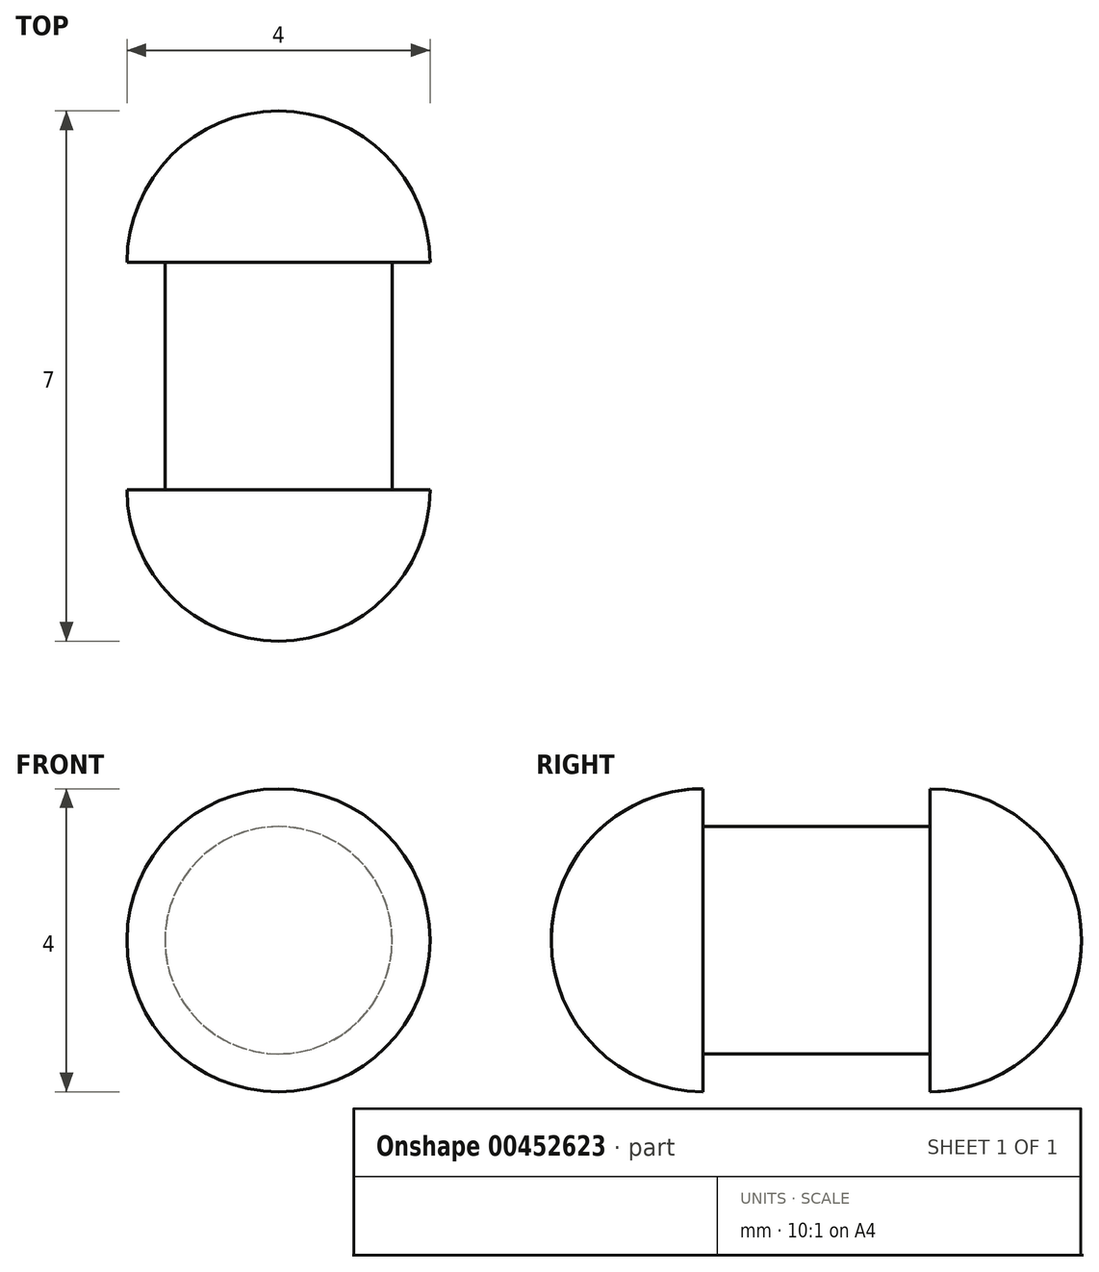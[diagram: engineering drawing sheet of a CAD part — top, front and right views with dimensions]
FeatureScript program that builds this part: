
annotation { "Feature Type Name" : "Feature", "Feature Type Description" : "" }
export const myFeature = defineFeature(function(context is Context, id is Id, definition is map)
    precondition{}
    {
        {
            var Q0;
            Q0=qCreatedBy(makeId("Front.planeOp"),FACE);
            var sketch = newSketch(context, id + "F0", { "sketchPlane" : qUnion([Q0])});
            skCircle(sketch, "E0", {"center": v(0, 0) * mm, "radius": 1.5 * mm});
            skSolve(sketch);
        }
        {
            var Q0;
            Q0 = qSketchRegion(id + "F0", true);
            extrude(context, id + "F1", {"entities" : qUnion([Q0]), "depth" : 3 * mm});
        }
        {
            var Q0;
            Q0=qCreatedBy(makeId("Right.planeOp"),FACE);
            var sketch = newSketch(context, id + "F2", { "sketchPlane" : qUnion([Q0])});
            skLineSegment(sketch, "E1", {"start": v(0, 0) * mm, "end": v(0, 2) * mm});
            skLineSegment(sketch, "E2", {"start": v(0, 0) * mm, "end": v(2, 0) * mm});
            skArc(sketch, "E3", {"start": v(0, 2) * mm, "mid": v(1.41, 1.41) * mm, "end": v(2, 0) * mm});
            skLineSegment(sketch, "E4", {"start": v(0, 0) * mm, "end": v(-3, 0) * mm, "construction": true});
            skLineSegment(sketch, "E5", {"start": v(-3, 0) * mm, "end": v(-5, 0) * mm});
            skArc(sketch, "E6", {"start": v(-5, 0) * mm, "mid": v(-4.41, 1.41) * mm, "end": v(-3, 2) * mm});
            skLineSegment(sketch, "E7", {"start": v(-3, 0) * mm, "end": v(-3, 2) * mm});
            skSolve(sketch);
        }
        {
            var Q0;
            Q0 = qSketchRegion(id + "F2", true);
            var Q1;
            Q1=sQuery(id+"F2.wireOp",EDGE,"E5");
            revolve(context, id + "F3", {"operationType" : NewBodyOperationType.ADD, "entities" : qUnion([Q0]), "axis" : qUnion([Q1]), "revolveType" : RevolveType.FULL});
        }
    });
